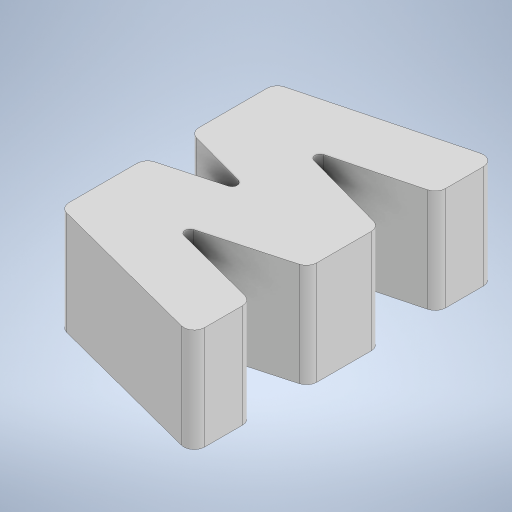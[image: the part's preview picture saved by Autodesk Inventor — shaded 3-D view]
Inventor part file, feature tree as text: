
AUTODESK INVENTOR PART (.ipt)
format: ipt  version: 2023 (Build 270158000, 158)  size: 392,192 bytes
history: native  units: mm
features: extrude x4, sketch x4, projected_geometry x3, other x2
ambient origin geometry x8: Origin, YZ Plane, XZ Plane, XY Plane, X Axis, Y Axis, Z Axis, Center Point
bodies: Body1 (feature_tree), Body2 (feature_tree)
feature tree (13):
  other  "contorno"
  extrude  "Extrusión1"  Depth=0.65mm
  extrude  "Extrusión2"  TaperAngle=30.0deg  [1 undecoded]
  extrude  "Extrusión3"  Depth=7.224mm
  extrude  "Extrusión4"  Depth=22.124mm
  sketch  "Boceto1"  dims[d8=13.0mm d9=0.0mm d17=0.65mm]
  sketch  "Boceto2"  dims[d41=1.3mm d42=30.0deg]
  projected_geometry  "Contorno proyectado1"
  other  "cavidad"
  sketch  "Boceto3"  dims[d43=30.0deg d44=7.224mm]
  projected_geometry  "Contorno proyectado2"
  sketch  "Boceto4"  dims[d47=24.887mm d48=22.124mm d50=8.661mm d51=14.064mm d52=1.2mm d53=13.0mm d54=0.0mm d55=3.4mm d56=0.0mm d57=3.4mm d58=0.0mm]
  projected_geometry  "Contorno proyectado3"
note: 1 required parameter value undecoded (feature->parameter linkage not recoverable at this tier; creation-order binding heuristic only, values carry confidence <= 0.55)
